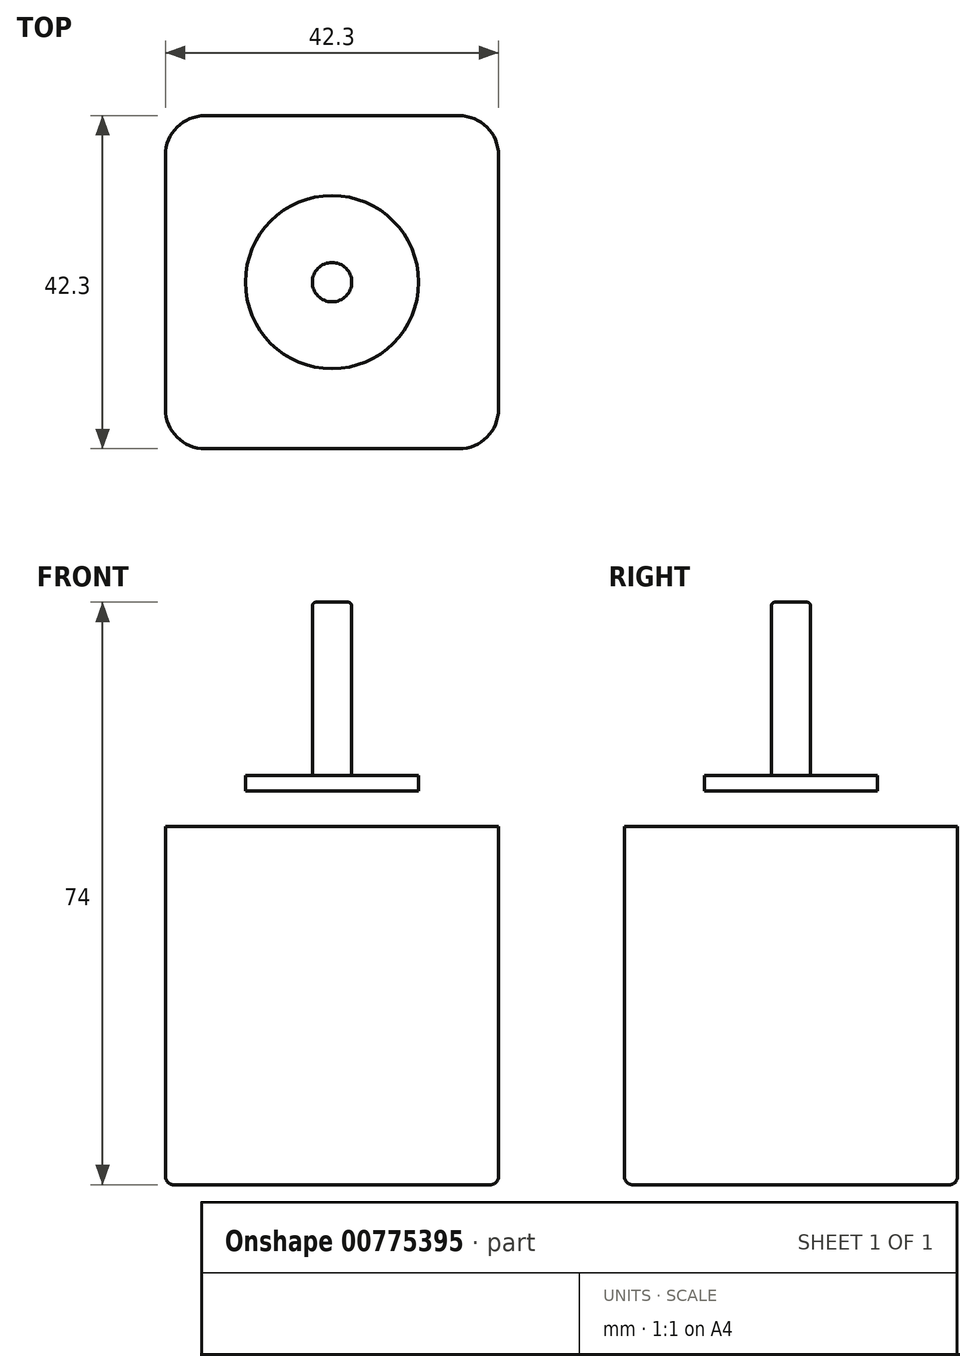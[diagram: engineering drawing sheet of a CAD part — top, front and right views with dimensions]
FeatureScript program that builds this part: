
annotation { "Feature Type Name" : "Feature", "Feature Type Description" : "" }
export const myFeature = defineFeature(function(context is Context, id is Id, definition is map)
    precondition{}
    {
        {
            assignVariable(context, id + "F0", {"name" : "Height", "anyValue" : 50});
        }
        {
            var Q0;
            Q0=qCreatedBy(makeId("Top.planeOp"),FACE);
            var sketch = newSketch(context, id + "F1", { "sketchPlane" : qUnion([Q0])});
            skLineSegment(sketch, "E0.bottom", {"start": v(-21.15, 21.15) * mm, "end": v(21.15, 21.15) * mm});
            skLineSegment(sketch, "E0.top", {"start": v(-21.15, -21.15) * mm, "end": v(21.15, -21.15) * mm});
            skLineSegment(sketch, "E0.left", {"start": v(-21.15, 21.15) * mm, "end": v(-21.15, -21.15) * mm});
            skLineSegment(sketch, "E0.right", {"start": v(21.15, 21.15) * mm, "end": v(21.15, -21.15) * mm});
            skLineSegment(sketch, "E1.bottom", {"start": v(-15.5, 15.5) * mm, "end": v(15.5, 15.5) * mm, "construction": true});
            skLineSegment(sketch, "E1.top", {"start": v(-15.5, -15.5) * mm, "end": v(15.5, -15.5) * mm, "construction": true});
            skLineSegment(sketch, "E1.left", {"start": v(-15.5, 15.5) * mm, "end": v(-15.5, -15.5) * mm, "construction": true});
            skLineSegment(sketch, "E1.right", {"start": v(15.5, 15.5) * mm, "end": v(15.5, -15.5) * mm, "construction": true});
            skCircle(sketch, "E2", {"center": v(-15.5, 15.5) * mm, "radius": 1.5 * mm});
            skCircle(sketch, "E3", {"center": v(15.5, 15.5) * mm, "radius": 1.5 * mm});
            skCircle(sketch, "E4", {"center": v(15.5, -15.5) * mm, "radius": 1.5 * mm});
            skCircle(sketch, "E5", {"center": v(-15.5, -15.5) * mm, "radius": 1.5 * mm});
            skCircle(sketch, "E6", {"center": v(0, 0) * mm, "radius": 11 * mm});
            skCircle(sketch, "E7", {"center": v(0, 0) * mm, "radius": 2.5 * mm});
            skSolve(sketch);
        }
        {
            var Q0;
            Q0=makeQuery(id+"F1.imprint","IMPRINT",FACE,{"disambiguationData":[TD([[makeQuery(id+"F1.imprint","IMPRINT",EDGE,{"derivedFrom":sQuery(id+"F1.wireOp",EDGE,"E2")}),1.0]])]});
            var Q1;
            Q1=makeQuery(id+"F1.imprint","IMPRINT",FACE,{"disambiguationData":[TD([[makeQuery(id+"F1.imprint","IMPRINT",EDGE,{"derivedFrom":sQuery(id+"F1.wireOp",EDGE,"E5")}),1.0]])]});
            var Q2;
            Q2=makeQuery(id+"F1.imprint","IMPRINT",FACE,{"disambiguationData":[TD([[makeQuery(id+"F1.imprint","IMPRINT",EDGE,{"derivedFrom":sQuery(id+"F1.wireOp",EDGE,"E4")}),1.0]])]});
            var Q3;
            Q3=makeQuery(id+"F1.imprint","IMPRINT",FACE,{"disambiguationData":[TD([[makeQuery(id+"F1.imprint","IMPRINT",EDGE,{"derivedFrom":sQuery(id+"F1.wireOp",EDGE,"E3")}),1.0]])]});
            var Q4;
            Q4=makeQuery(id+"F1.imprint","IMPRINT",FACE,{"disambiguationData":[TD([[makeQuery(id+"F1.imprint","IMPRINT",EDGE,{"derivedFrom":sQuery(id+"F1.wireOp",EDGE,"E0.bottom")}),-1.0]])]});
            var Q5;
            Q5=makeQuery(id+"F1.imprint","IMPRINT",FACE,{"disambiguationData":[TD([[makeQuery(id+"F1.imprint","IMPRINT",EDGE,{"derivedFrom":sQuery(id+"F1.wireOp",EDGE,"E6")}),1.0]])]});
            var Q6;
            Q6=makeQuery(id+"F1.imprint","IMPRINT",FACE,{"disambiguationData":[TD([[makeQuery(id+"F1.imprint","IMPRINT",EDGE,{"derivedFrom":sQuery(id+"F1.wireOp",EDGE,"E7")}),1.0]])]});
            extrude(context, id + "F2", {"entities" : qUnion([Q0, Q1, Q2, Q3, Q4, Q5, Q6]), "depth" : (getVariable(context, 'Height') - 4.5) * mm, "offsetDistance" : 25 * mm});
        }
        {
            var Q0;
            Q0=makeQuery(id+"F1.imprint","IMPRINT",FACE,{"disambiguationData":[TD([[makeQuery(id+"F1.imprint","IMPRINT",EDGE,{"derivedFrom":sQuery(id+"F1.wireOp",EDGE,"E6")}),1.0]])]});
            var Q1;
            Q1=makeQuery(id+"F1.imprint","IMPRINT",FACE,{"disambiguationData":[TD([[makeQuery(id+"F1.imprint","IMPRINT",EDGE,{"derivedFrom":sQuery(id+"F1.wireOp",EDGE,"E7")}),1.0]])]});
            extrude(context, id + "F3", {"entities" : qUnion([Q0, Q1]), "operationType" : NewBodyOperationType.ADD, "depth" : (getVariable(context, 'Height') + 2) * mm, "offsetDistance" : 25 * mm, "hasSecondDirection" : true, "secondDirectionOppositeDirection" : false, "secondDirectionDepth" : (getVariable(context, 'Height')) * mm});
        }
        {
            var Q0;
            Q0=makeQuery(id+"F1.imprint","IMPRINT",FACE,{"disambiguationData":[TD([[makeQuery(id+"F1.imprint","IMPRINT",EDGE,{"derivedFrom":sQuery(id+"F1.wireOp",EDGE,"E7")}),1.0]])]});
            extrude(context, id + "F4", {"entities" : qUnion([Q0]), "operationType" : NewBodyOperationType.ADD, "depth" : (getVariable(context, 'Height') + 24) * mm, "offsetDistance" : 25 * mm, "hasSecondDirection" : true, "secondDirectionOppositeDirection" : false, "secondDirectionDepth" : (getVariable(context, 'Height') + 2) * mm});
        }
        {
            var Q0;
            Q0=makeQuery(id+"F4.opExtrude","CAP_EDGE",EDGE,{"disambiguationData":[OSD([sQuery(id+"F1.wireOp",EDGE,"E7")])],"isStart":false});
            fillet(context, id + "F5", {"entities" : qUnion([Q0]), "radius" : 0.5 * mm, "tangentPropagation" : true, "allowEdgeOverflow" : false});
        }
        {
            var Q0;
            {var subQ0=sQuery(id+"F1.wireOp",EDGE,"E0.left");var subQ1=sQuery(id+"F1.wireOp",EDGE,"E0.top");Q0=makeQuery(id+"FfQy2iOukyVLp7R_1.boolean.opBoolean","MERGE",EDGE,{"derivedFrom":[makeQuery(id+"F2.opExtrude","SWEPT_EDGE",EDGE,{"disambiguationData":[OSD([subQ1,subQ0])]}),makeQuery(id+"FfQy2iOukyVLp7R_1.opExtrude","SWEPT_EDGE",EDGE,{"disambiguationData":[OSD([subQ1,subQ0])]})]});}
            var Q1;
            {var subQ0=sQuery(id+"F1.wireOp",EDGE,"E0.left");var subQ1=sQuery(id+"F1.wireOp",EDGE,"E0.bottom");Q1=makeQuery(id+"FfQy2iOukyVLp7R_1.boolean.opBoolean","MERGE",EDGE,{"derivedFrom":[makeQuery(id+"F2.opExtrude","SWEPT_EDGE",EDGE,{"disambiguationData":[OSD([subQ1,subQ0])]}),makeQuery(id+"FfQy2iOukyVLp7R_1.opExtrude","SWEPT_EDGE",EDGE,{"disambiguationData":[OSD([subQ1,subQ0])]})]});}
            var Q2;
            {var subQ0=sQuery(id+"F1.wireOp",EDGE,"E0.right");var subQ1=sQuery(id+"F1.wireOp",EDGE,"E0.bottom");Q2=makeQuery(id+"FfQy2iOukyVLp7R_1.boolean.opBoolean","MERGE",EDGE,{"derivedFrom":[makeQuery(id+"F2.opExtrude","SWEPT_EDGE",EDGE,{"disambiguationData":[OSD([subQ1,subQ0])]}),makeQuery(id+"FfQy2iOukyVLp7R_1.opExtrude","SWEPT_EDGE",EDGE,{"disambiguationData":[OSD([subQ1,subQ0])]})]});}
            var Q3;
            {var subQ0=sQuery(id+"F1.wireOp",EDGE,"E0.right");var subQ1=sQuery(id+"F1.wireOp",EDGE,"E0.top");Q3=makeQuery(id+"FfQy2iOukyVLp7R_1.boolean.opBoolean","MERGE",EDGE,{"derivedFrom":[makeQuery(id+"F2.opExtrude","SWEPT_EDGE",EDGE,{"disambiguationData":[OSD([subQ1,subQ0])]}),makeQuery(id+"FfQy2iOukyVLp7R_1.opExtrude","SWEPT_EDGE",EDGE,{"disambiguationData":[OSD([subQ1,subQ0])]})]});}
            fillet(context, id + "F6", {"entities" : qUnion([Q0, Q1, Q2, Q3]), "radius" : 5 * mm, "tangentPropagation" : true, "allowEdgeOverflow" : false});
        }
        {
            var Q0;
            {var subQ0=sQuery(id+"F1.wireOp",EDGE,"E0.left");var subQ1=sQuery(id+"F1.wireOp",EDGE,"E0.bottom");Q0=makeQuery(id+"F6.opFillet","BLEND_EDGE",EDGE,{"blendedFrom":[makeQuery(id+"FfQy2iOukyVLp7R_1.boolean.opBoolean","MERGE",EDGE,{"derivedFrom":[makeQuery(id+"F2.opExtrude","SWEPT_EDGE",EDGE,{"disambiguationData":[OSD([subQ1,subQ0])]}),makeQuery(id+"FfQy2iOukyVLp7R_1.opExtrude","SWEPT_EDGE",EDGE,{"disambiguationData":[OSD([subQ1,subQ0])]})]}),makeQuery(id+"FfQy2iOukyVLp7R_1.opExtrude","CAP_FACE",FACE,{"disambiguationData":[OSD([subQ1,sQuery(id+"F1.wireOp",EDGE,"E0.top"),subQ0,sQuery(id+"F1.wireOp",EDGE,"E0.right"),sQuery(id+"F1.wireOp",EDGE,"E2"),sQuery(id+"F1.wireOp",EDGE,"E3"),sQuery(id+"F1.wireOp",EDGE,"E4"),sQuery(id+"F1.wireOp",EDGE,"E5")])],"isStart":false})],"blendedInto":[makeQuery(id+"FfQy2iOukyVLp7R_1.opExtrude","CAP_FACE",FACE,{"disambiguationData":[OSD([subQ1,sQuery(id+"F1.wireOp",EDGE,"E0.top"),subQ0,sQuery(id+"F1.wireOp",EDGE,"E0.right"),sQuery(id+"F1.wireOp",EDGE,"E2"),sQuery(id+"F1.wireOp",EDGE,"E3"),sQuery(id+"F1.wireOp",EDGE,"E4"),sQuery(id+"F1.wireOp",EDGE,"E5")])],"isStart":false})]});}
            var Q1;
            Q1=makeQuery(id+"F2.opExtrude","CAP_FACE",FACE,{"disambiguationData":[OSD([sQuery(id+"F1.wireOp",EDGE,"E0.bottom"),sQuery(id+"F1.wireOp",EDGE,"E0.top"),sQuery(id+"F1.wireOp",EDGE,"E0.left"),sQuery(id+"F1.wireOp",EDGE,"E0.right")])],"isStart":true});
            fillet(context, id + "F7", {"entities" : qUnion([Q0, Q1]), "radius" : 1 * mm, "tangentPropagation" : true, "allowEdgeOverflow" : false});
        }
    });
